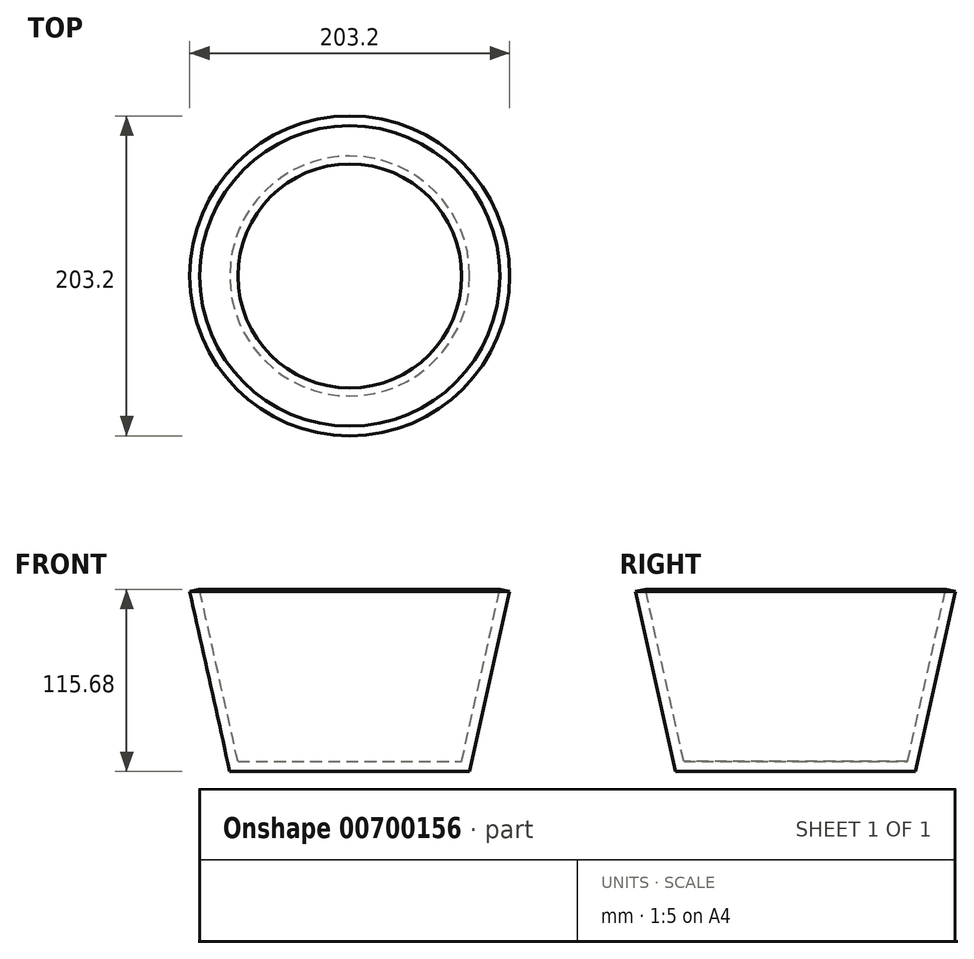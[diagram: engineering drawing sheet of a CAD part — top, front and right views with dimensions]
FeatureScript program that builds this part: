
annotation { "Feature Type Name" : "Feature", "Feature Type Description" : "" }
export const myFeature = defineFeature(function(context is Context, id is Id, definition is map)
    precondition{}
    {
        {
            var Q0;
            Q0=qCreatedBy(makeId("Front.planeOp"),FACE);
            var sketch = newSketch(context, id + "F0", { "sketchPlane" : qUnion([Q0])});
            skLineSegment(sketch, "E0", {"start": v(0, 0) * mm, "end": v(76.2, 0) * mm});
            skLineSegment(sketch, "E1", {"start": v(76.2, 0) * mm, "end": v(76.2, 114.3) * mm, "construction": true});
            skLineSegment(sketch, "E2", {"start": v(76.2, 114.3) * mm, "end": v(101.6, 114.3) * mm, "construction": true});
            skLineSegment(sketch, "E3", {"start": v(101.6, 114.3) * mm, "end": v(76.2, 0) * mm});
            skLineSegment(sketch, "E4.0", {"start": v(95.4, 115.68) * mm, "end": v(71.1, 6.35) * mm});
            skLineSegment(sketch, "E5.0", {"start": v(0, 6.35) * mm, "end": v(71.1, 6.35) * mm});
            skLineSegment(sketch, "E6", {"start": v(0, 6.35) * mm, "end": v(0, 0) * mm});
            skLineSegment(sketch, "E7", {"start": v(95.4, 115.68) * mm, "end": v(101.6, 114.3) * mm});
            skSolve(sketch);
        }
        {
            var Q0;
            Q0=qCreatedBy(makeId("Front.planeOp"),FACE);
            var sketch = newSketch(context, id + "F1", { "sketchPlane" : qUnion([Q0])});
            skLineSegment(sketch, "E8", {"start": v(0, 0) * mm, "end": v(0, 158.54) * mm, "construction": true});
            skSolve(sketch);
        }
        {
            var Q0;
            Q0=makeQuery(id+"F0.imprint","IMPRINT",FACE,{"disambiguationData":[TD([[makeQuery(id+"F0.imprint","IMPRINT",EDGE,{"derivedFrom":sQuery(id+"F0.wireOp",EDGE,"E0")}),1.0]])]});
            var Q1;
            Q1=sQuery(id+"F1.wireOp",EDGE,"E8");
            revolve(context, id + "F2", {"entities" : qUnion([Q0]), "axis" : qUnion([Q1]), "revolveType" : RevolveType.FULL});
        }
    });
